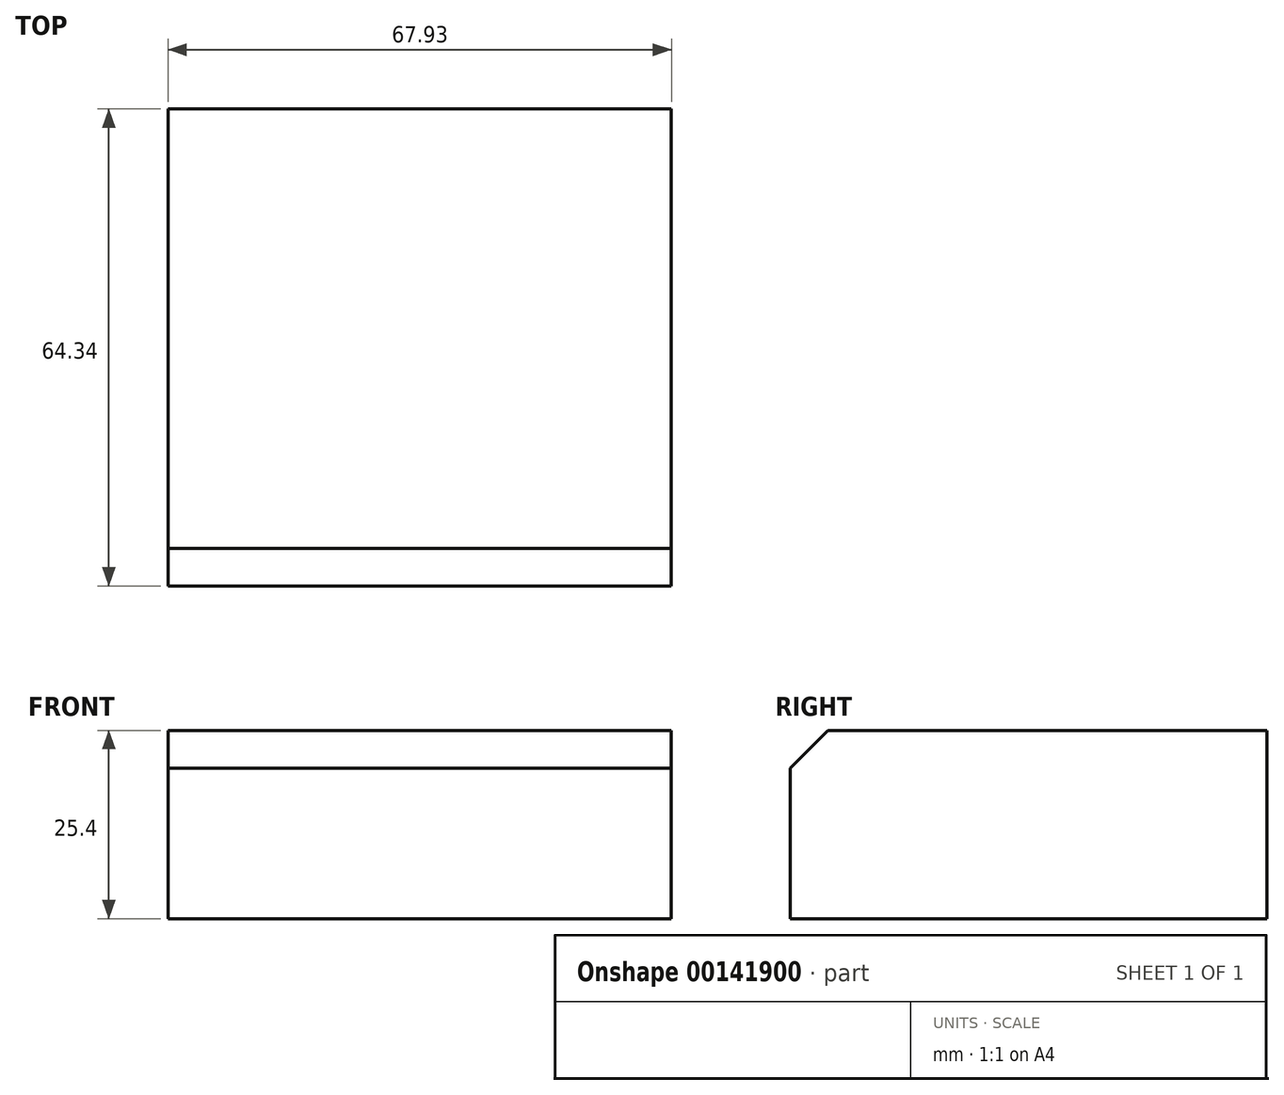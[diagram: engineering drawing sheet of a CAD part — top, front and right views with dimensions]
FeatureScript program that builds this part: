
annotation { "Feature Type Name" : "Feature", "Feature Type Description" : "" }
export const myFeature = defineFeature(function(context is Context, id is Id, definition is map)
    precondition{}
    {
        {
            var Q0;
            Q0=qCreatedBy(makeId("Top.planeOp"),FACE);
            var sketch = newSketch(context, id + "F0", { "sketchPlane" : qUnion([Q0])});
            skLineSegment(sketch, "E0.bottom", {"start": v(-25.2, 32.62) * mm, "end": v(42.74, 32.62) * mm});
            skLineSegment(sketch, "E0.top", {"start": v(8.77, -31.72) * mm, "end": v(42.74, -31.72) * mm});
            skLineSegment(sketch, "E0.left", {"start": v(-25.2, 32.62) * mm, "end": v(-25.2, -31.72) * mm});
            skLineSegment(sketch, "E0.right", {"start": v(42.74, 32.62) * mm, "end": v(42.74, -31.72) * mm});
            skPoint(sketch, "E1", {"position": v(8.77, -31.72) * mm});
            skLineSegment(sketch, "E2", {"start": v(-25.2, -31.72) * mm, "end": v(8.77, -31.72) * mm});
            skSolve(sketch);
        }
        {
            var Q0;
            Q0 = qSketchRegion(id + "F0", true);
            extrude(context, id + "F1", {"entities" : qUnion([Q0]), "depth" : 25.4 * mm});
        }
        {
            var Q0;
            Q0=makeQuery(id+"F1.opExtrude","CAP_EDGE",EDGE,{"disambiguationData":[OSD([sQuery(id+"F0.wireOp",EDGE,"E0.top")])],"isStart":false});
            chamfer(context, id + "F2", {"entities" : qUnion([Q0]), "width" : 5.08 * mm, "tangentPropagation" : true});
        }
    });
